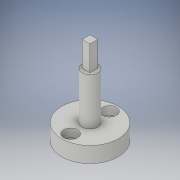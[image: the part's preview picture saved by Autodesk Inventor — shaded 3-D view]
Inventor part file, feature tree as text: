
AUTODESK INVENTOR PART (.ipt)
format: ipt  version: 2019 (Build 230136000, 136)  size: 130,560 bytes
history: native  units: in
note: dims shown in document units (in); Inventor stores cm internally (conversion verified against a paired STEP export)
features: sketch x4, extrude x3, hole x1
ambient origin geometry x8: Origin, YZ Plane, XZ Plane, XY Plane, X Axis, Y Axis, Z Axis, Center Point
bodies: Solid1 (feature_tree)
feature tree (8):
  extrude  "Extrusion1"  Depth=0.25in TaperAngle=0.0deg
  hole  "Hole1"  [1 undecoded]
  extrude  "Extrusion2"  Depth=0.25in
  extrude  "Extrusion3"  Depth=0.125in
  sketch  "Sketch1"  dims[d0=0.9in d1=0.25in d2=0.0in]
  sketch  "Sketch2"  dims[d3=0.6185in d4=0.3093in]
  sketch  "Sketch3"  dims[d5=0.134in d6=0.75in d7=0.225in d8=0.135in d9=0.5635in d10=0.4in d11=0.0in d12=0.25in]
  sketch  "Sketch4"  dims[d13=0.75in d14=0.0in d15=0.125in d16=0.125in d17=0.0625in d18=0.0625in d19=0.4in d20=0.0in d21=0.3093in d22=0.0in]
note: 1 required parameter value undecoded (feature->parameter linkage not recoverable at this tier; creation-order binding heuristic only, values carry confidence <= 0.55)
